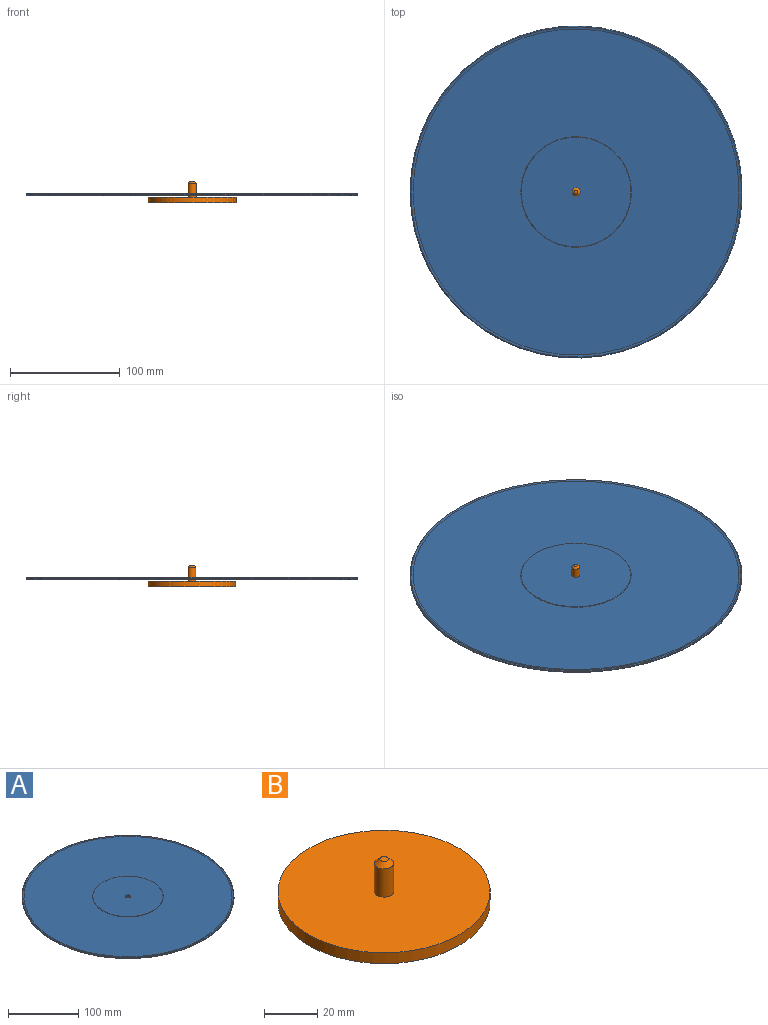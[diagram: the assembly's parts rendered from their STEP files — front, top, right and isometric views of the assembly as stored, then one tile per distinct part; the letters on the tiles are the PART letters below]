
ASSEMBLY  parts=2 mates=1
PART A: 12 faces, bbox 302.4x302.4x2.3 mm
  f0: cone r=150.4mm half-angle=79.1deg, axis (0,0,1), area 1894.3mm2, adj f1,f11
  f1: cone r=151.2mm half-angle=46.1deg, axis (0,0,-1), area 1052.1mm2, adj f0,f2
  f2: cylinder r=151.2mm len=302.4mm, axis (0,0,-1), area 722mm2, adj f1,f3
  f3: cone r=151.2mm half-angle=46.1deg, axis (0,0,1), area 1052.1mm2, adj f2,f4
  f4: cone r=150.4mm half-angle=79.1deg, axis (0,0,-1), area 1894.3mm2, adj f3,f5
  f5: plane 296.84x296.84mm, normal (0,0,-1), area 61229.2mm2, adj f4,f6
  f6: cone r=50mm half-angle=45deg, axis (0,0,1), area 169.5mm2, adj f5,f7
  f7: plane 100x100mm, normal (0,0,-1), area 7812.5mm2, adj f6,f8
  f8: cylinder r=3.63mm len=7.26mm, axis (0,0,-1), area 52.5mm2, adj f7,f9
  f9: plane 100x100mm, normal (0,0,1), area 7812.5mm2, adj f8,f10
  f10: cone r=50mm half-angle=45deg, axis (0,0,-1), area 169.5mm2, adj f9,f11
  f11: plane 296.84x296.84mm, normal (0,0,1), area 61229.2mm2, adj f0,f10
PART B: 11 faces, bbox 80x80x20 mm
  f0: cylinder r=40mm len=80mm, axis (0,0,-1), area 1256.6mm2, adj f1,f2
  f1: plane 80x80mm, normal (0,0,1), area 4985.1mm2, adj f0,f3
  f2: plane 80x80mm, normal (0,0,-1), area 4976.3mm2, adj f0,f6
  f3: cylinder r=3.63mm len=13mm, axis (0,0,-1), area 296.7mm2, adj f1,f5
  f4: plane 3.26x3.26mm, normal (0,0,1), area 8.4mm2, adj f5
  f5: cone r=1.63mm half-angle=45deg, axis (0,0,-1), area 46.8mm2, adj f3,f4
  f6: cylinder r=4mm len=8mm, axis (0,0,-1), area 75.4mm2, adj f2,f7
  f7: plane 8x8mm, normal (0,0,-1), area 22mm2, adj f6,f10
  f8: cylinder r=1.5mm len=8.5mm, axis (0,0,-1), area 80.1mm2, adj f9,f10
  f9: plane 3x3mm, normal (0,0,-1), area 7.1mm2, adj f8
  f10: cone r=1.5mm half-angle=45deg, axis (0,0,-1), area 30mm2, adj f7,f8
PLACE A t=(-13.58,-4.85,18.81)mm
PLACE B t=(-13.58,-4.85,10.93)mm
MATE slider A.f0 <-> B.f0  axis (0,0,-1) through (-13.58,-4.85,17.66)mm
